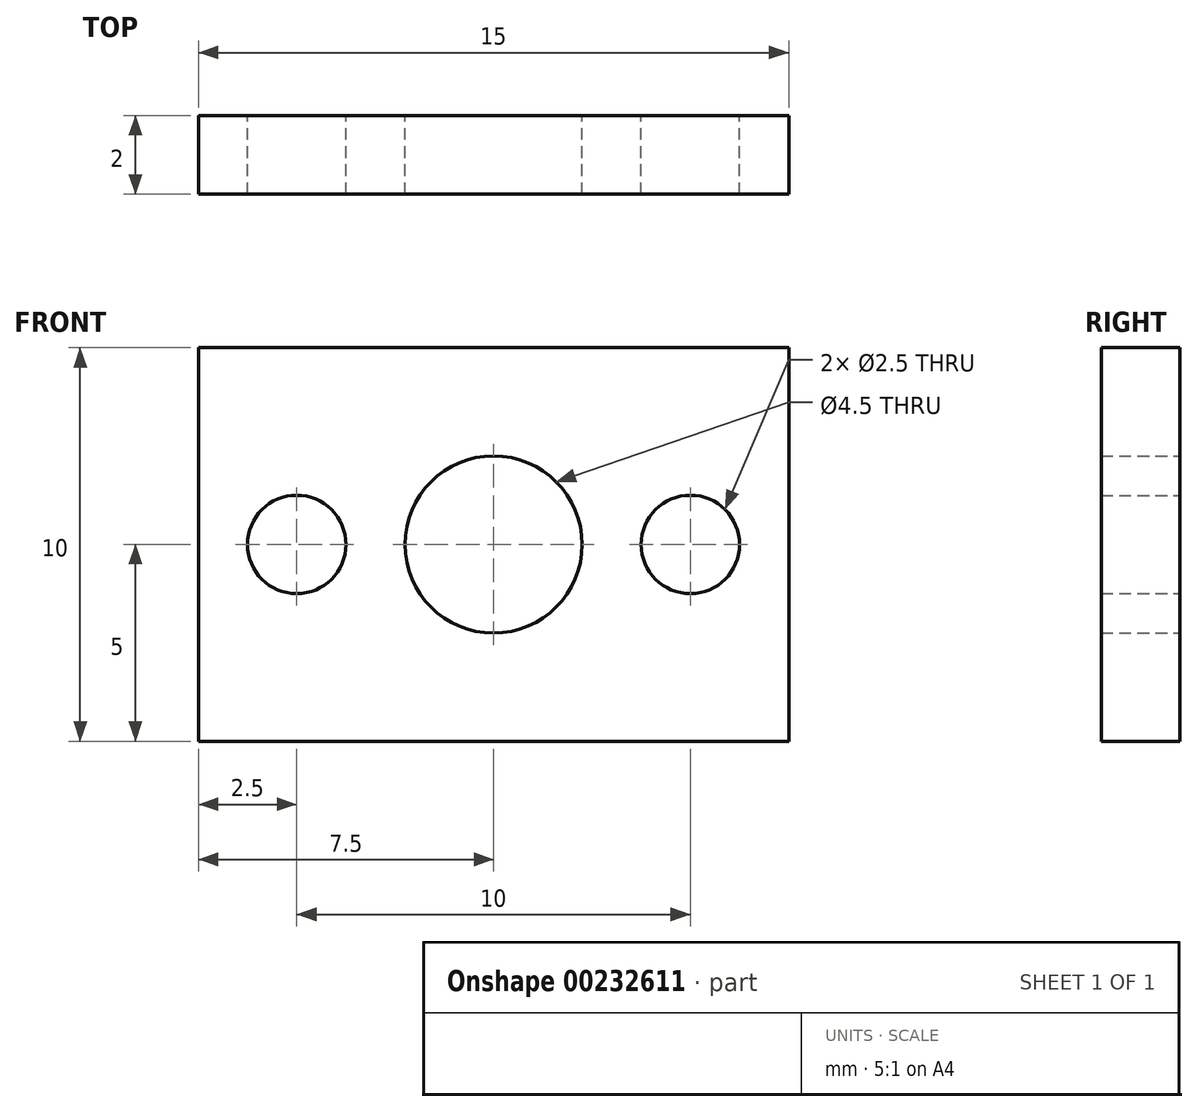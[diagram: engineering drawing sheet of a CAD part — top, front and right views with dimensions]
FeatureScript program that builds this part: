
annotation { "Feature Type Name" : "Feature", "Feature Type Description" : "" }
export const myFeature = defineFeature(function(context is Context, id is Id, definition is map)
    precondition{}
    {
        {
            var Q0;
            Q0=qCreatedBy(makeId("Front.planeOp"),FACE);
            var sketch = newSketch(context, id + "F0", { "sketchPlane" : qUnion([Q0])});
            skLineSegment(sketch, "E0.bottom", {"start": v(0, 0) * mm, "end": v(15, 0) * mm});
            skLineSegment(sketch, "E0.top", {"start": v(0, 10) * mm, "end": v(15, 10) * mm});
            skLineSegment(sketch, "E0.left", {"start": v(0, 0) * mm, "end": v(0, 10) * mm});
            skLineSegment(sketch, "E0.right", {"start": v(15, 0) * mm, "end": v(15, 10) * mm});
            skCircle(sketch, "E1", {"center": v(7.5, 5) * mm, "radius": 2.25 * mm});
            skCircle(sketch, "E2", {"center": v(2.5, 5) * mm, "radius": 1.25 * mm});
            skCircle(sketch, "E3", {"center": v(12.5, 5) * mm, "radius": 1.25 * mm});
            skSolve(sketch);
        }
        {
            var Q0;
            Q0 = qSketchRegion(id + "F0", true);
            extrude(context, id + "F1", {"entities" : qUnion([Q0]), "depth" : 2 * mm});
        }
    });
